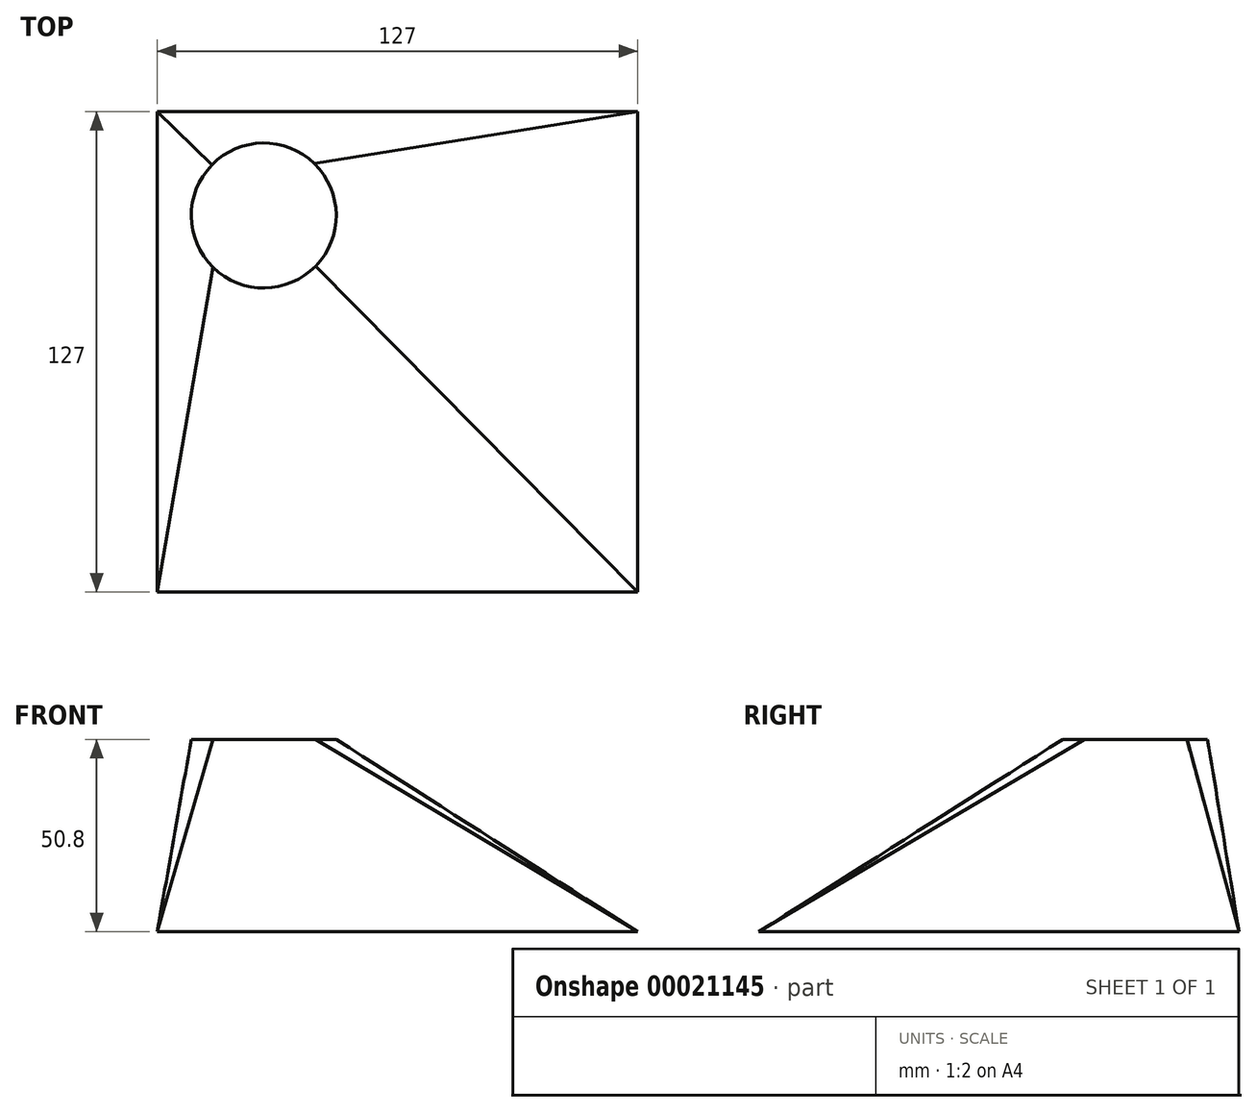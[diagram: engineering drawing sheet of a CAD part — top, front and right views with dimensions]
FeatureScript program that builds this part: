
annotation { "Feature Type Name" : "Feature", "Feature Type Description" : "" }
export const myFeature = defineFeature(function(context is Context, id is Id, definition is map)
    precondition{}
    {
        {
            var Q0;
            Q0=qCreatedBy(makeId("Top.planeOp"),FACE);
            var sketch = newSketch(context, id + "F0", { "sketchPlane" : qUnion([Q0])});
            skLineSegment(sketch, "E0.bottom", {"start": v(0, 0) * mm, "end": v(127, 0) * mm});
            skLineSegment(sketch, "E0.top", {"start": v(0, -127) * mm, "end": v(127, -127) * mm});
            skLineSegment(sketch, "E0.left", {"start": v(0, 0) * mm, "end": v(0, -127) * mm});
            skLineSegment(sketch, "E0.right", {"start": v(127, 0) * mm, "end": v(127, -127) * mm});
            skSolve(sketch);
        }
        {
            var Q0;
            Q0=qCreatedBy(makeId("Top.planeOp"),FACE);
            cPlane(context, id + "F1", {"entities" : qUnion([Q0]), "cplaneType" : CPlaneType.OFFSET, "offset" : 50.8 * mm, "width" : 152.4 * mm, "height" : 152.4 * mm});
        }
        {
            var Q0;
            Q0=qCreatedBy(id+"F1.planeOp",FACE);
            var sketch = newSketch(context, id + "F2", { "sketchPlane" : qUnion([Q0])});
            skCircle(sketch, "E1", {"center": v(28.16, -27.48) * mm, "radius": 19.16 * mm});
            skSolve(sketch);
        }
        {
            var Q0;
            Q0=makeQuery(id+"F2.imprint","IMPRINT",FACE,{"disambiguationData":[TD([[makeQuery(id+"F2.imprint","IMPRINT",EDGE,{"derivedFrom":sQuery(id+"F2.wireOp",EDGE,"E1")}),1.0]])]});
            var Q1;
            Q1=makeQuery(id+"F0.imprint","IMPRINT",FACE,{"disambiguationData":[TD([[makeQuery(id+"F0.imprint","IMPRINT",EDGE,{"derivedFrom":sQuery(id+"F0.wireOp",EDGE,"E0.bottom")}),-1.0]])]});
            loft(context, id + "F3", {"sheetProfilesArray" : [{ "sheetProfileEntities" : qUnion([Q0]) }, { "sheetProfileEntities" : qUnion([Q1]) }]});
        }
    });
